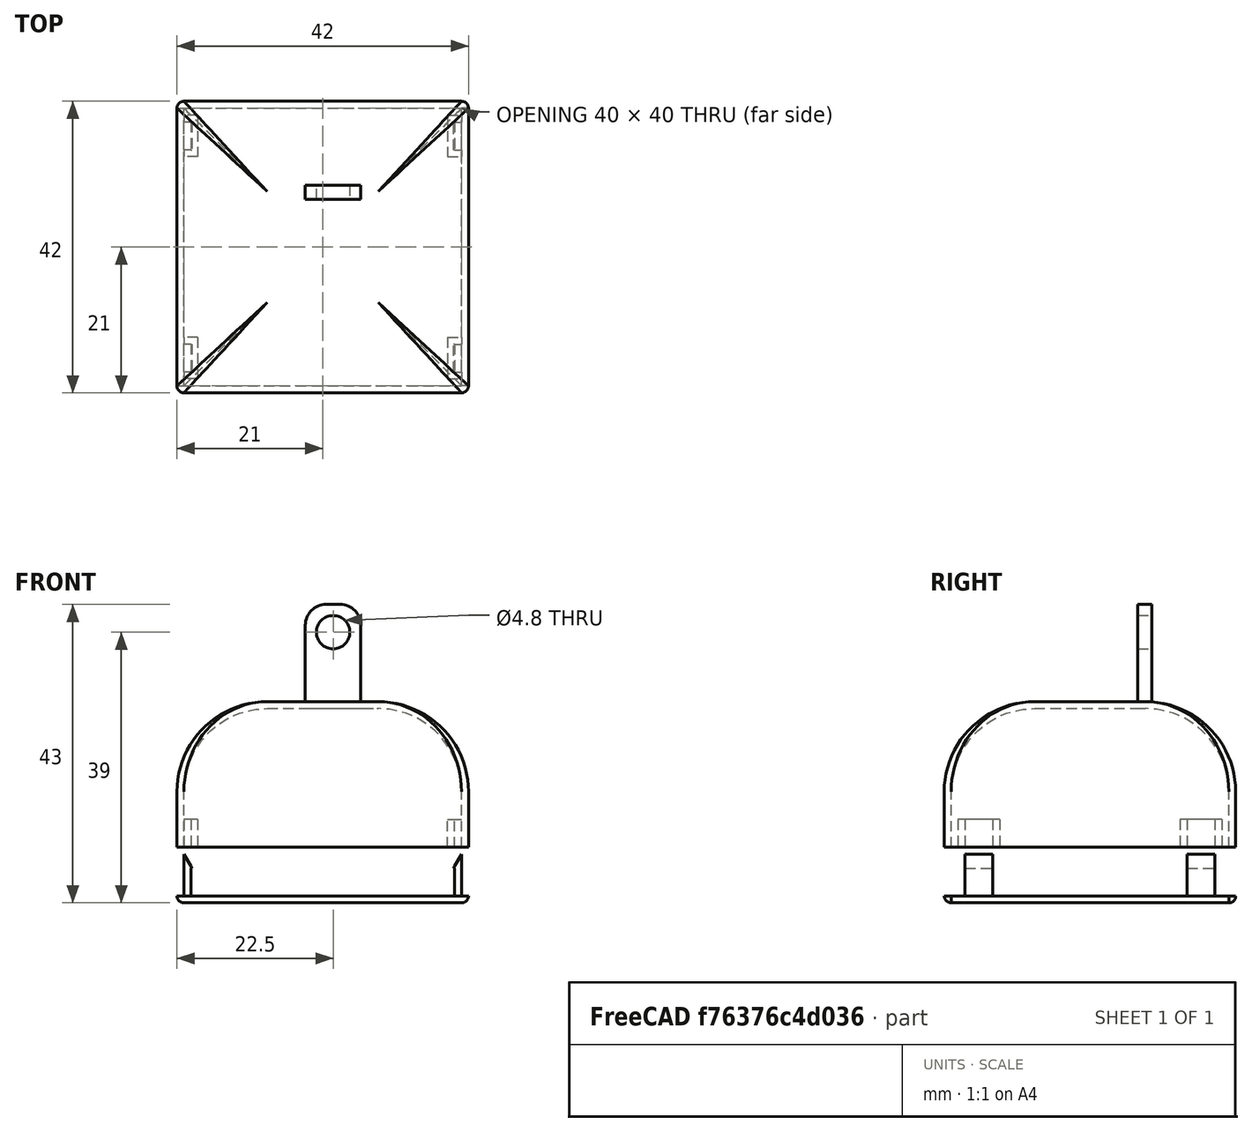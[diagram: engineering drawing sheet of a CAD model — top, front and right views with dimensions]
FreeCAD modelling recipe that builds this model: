
FCSTD DOCUMENT  (FreeCAD 0.21R33771 (Git))
Label: paw draft
License: All rights reserved
LicenseURL: https://en.wikipedia.org/wiki/All_rights_reserved
objects: Part::Box×24, Part::Cut×9, Part::MultiFuse×6, Part::Fillet×2, Part::Thickness×2, Part::Cylinder×1, Part::MultiCommon×1
note: 45 computed .brp shape members not serialized (recipe doc carries the construction recipe); baked Part::Feature solids carry a one-line shape summary decoded from their .brp

FEATURE [Part::Box] Box053  label="azeazeaze002"
  AttacherType = Attacher::AttachEngine3D
  Height = 15
  Length = 8
  Width = 2
FEATURE [Part::Box] Box055  label="Cube037"
  AttacherType = Attacher::AttachEngine3D
  Height = 1
  Length = 42
  Placement = pos=(-1,-1,-1) rot=(0,0,1;0rad)
  Width = 42
FEATURE [Part::Box] Box056  label="paw001"
  AttacherType = Attacher::AttachEngine3D
  Height = 20
  Length = 40
  Width = 40
FEATURE [Part::Box] Box057  label="Cube038"
  AttacherType = Attacher::AttachEngine3D
  Height = 6
  Length = 2
  Width = 4
FEATURE [Part::Box] Box058  label="Cube039"
  AttacherType = Attacher::AttachEngine3D
  Height = 4
  Length = 1
  Placement = pos=(1,0,1) rot=(0,0,1;0rad)
  Width = 4
FEATURE [Part::Box] Box059  label="Cube040"
  AttacherType = Attacher::AttachEngine3D
  Height = 6
  Length = 2
  Width = 4
FEATURE [Part::Box] Box060  label="Cube041"
  AttacherType = Attacher::AttachEngine3D
  Height = 4
  Length = 1
  Placement = pos=(1,0,1) rot=(0,0,1;0rad)
  Width = 4
FEATURE [Part::Box] Box061  label="Cube042"
  AttacherType = Attacher::AttachEngine3D
  Height = 6
  Length = 2
  Width = 4
FEATURE [Part::Box] Box062  label="Cube043"
  AttacherType = Attacher::AttachEngine3D
  Height = 4
  Length = 1
  Placement = pos=(1,0,1) rot=(0,0,1;0rad)
  Width = 4
FEATURE [Part::Box] Box063  label="Cube044"
  AttacherType = Attacher::AttachEngine3D
  Height = 6
  Length = 2
  Width = 4
FEATURE [Part::Box] Box064  label="Cube045"
  AttacherType = Attacher::AttachEngine3D
  Height = 4
  Length = 1
  Placement = pos=(1,0,1) rot=(0,0,1;0rad)
  Width = 4
FEATURE [Part::Box] Box065  label="paw002"
  AttacherType = Attacher::AttachEngine3D
  Height = 20
  Length = 40
  Width = 40
FEATURE [Part::Box] Box066  label="Cube046"
  AttacherType = Attacher::AttachEngine3D
  Height = 4
  Length = 2
  Placement = pos=(1,0,1) rot=(0,0,-1;0.523599rad)
  Width = 3
FEATURE [Part::Box] Box067  label="Cube047"
  AttacherType = Attacher::AttachEngine3D
  Height = 4
  Length = 1
  Placement = pos=(1,0,1) rot=(0,0,1;0rad)
  Width = 6
FEATURE [Part::Box] Box068  label="Cube048"
  AttacherType = Attacher::AttachEngine3D
  Height = 4
  Length = 1.2
  Placement = pos=(1,0,1) rot=(0,0,1;0rad)
  Width = 2
FEATURE [Part::Box] Box069  label="Cube049"
  AttacherType = Attacher::AttachEngine3D
  Height = 4
  Length = 2
  Placement = pos=(1,0,1) rot=(0,0,-1;0.523599rad)
  Width = 3
FEATURE [Part::Box] Box070  label="Cube050"
  AttacherType = Attacher::AttachEngine3D
  Height = 4
  Length = 1
  Placement = pos=(1,0,1) rot=(0,0,1;0rad)
  Width = 6
FEATURE [Part::Box] Box071  label="Cube051"
  AttacherType = Attacher::AttachEngine3D
  Height = 4
  Length = 1.2
  Placement = pos=(1,0,1) rot=(0,0,1;0rad)
  Width = 2
FEATURE [Part::Box] Box072  label="Cube052"
  AttacherType = Attacher::AttachEngine3D
  Height = 4
  Length = 2
  Placement = pos=(1,0,1) rot=(0,0,-1;0.523599rad)
  Width = 3
FEATURE [Part::Box] Box073  label="Cube053"
  AttacherType = Attacher::AttachEngine3D
  Height = 4
  Length = 1
  Placement = pos=(1,0,1) rot=(0,0,1;0rad)
  Width = 6
FEATURE [Part::Box] Box074  label="Cube054"
  AttacherType = Attacher::AttachEngine3D
  Height = 4
  Length = 1.2
  Placement = pos=(1,0,1) rot=(0,0,1;0rad)
  Width = 2
FEATURE [Part::Box] Box075  label="Cube055"
  AttacherType = Attacher::AttachEngine3D
  Height = 4
  Length = 2
  Placement = pos=(1,0,1) rot=(0,0,-1;0.523599rad)
  Width = 3
FEATURE [Part::Box] Box076  label="Cube056"
  AttacherType = Attacher::AttachEngine3D
  Height = 4
  Length = 1
  Placement = pos=(1,0,1) rot=(0,0,1;0rad)
  Width = 6
FEATURE [Part::Box] Box077  label="Cube057"
  AttacherType = Attacher::AttachEngine3D
  Height = 4
  Length = 1.2
  Placement = pos=(1,0,1) rot=(0,0,1;0rad)
  Width = 2
FEATURE [Part::Cut] Cut024
  Base = -> Box057
  Placement = pos=(38,7,1) rot=(1,0,0;1.5708rad)
  Tool = -> Box058
FEATURE [Part::Cut] Cut025
  Base = -> Box059
  Placement = pos=(38,39,1) rot=(1,0,0;1.5708rad)
  Tool = -> Box060
FEATURE [Part::Cut] Cut026
  Base = -> Box061
  Placement = pos=(2,7,5) rot=(0,0.707107,-0.707107;3.14159rad)
  Tool = -> Box062
FEATURE [Part::Cut] Cut027
  Base = -> Box063
  Placement = pos=(2,39,5) rot=(0,0.707107,-0.707107;3.14159rad)
  Tool = -> Box064
FEATURE [Part::Cylinder] Cylinder014  label="Cylindre014"
  Angle = 360
  AttacherType = Attacher::AttachEngine3D
  FirstAngle = 0
  Height = 10
  Placement = pos=(4,4,11) rot=(1,0,0;1.5708rad)
  Radius = 2.4
  SecondAngle = 0
FEATURE [Part::Cut] Cut022
  Base = -> Box053
  Placement = pos=(17.5,26.9,86) rot=(0,0,1;0rad)
  Tool = -> Cylinder014
FEATURE [Part::Fillet] Fillet005
  Base = -> Cut022
  Edges = 2 edges r=3: [Edge2,Edge10]
  Placement = pos=(0,0,-65) rot=(0,0,1;0rad)
FEATURE [Part::Fillet] Fillet007
  Base = -> Box056
  Edges = 4 edges r=12: [Edge2,Edge6,Edge10,Edge12]
  Placement = pos=(0,0,1) rot=(0,0,1;0rad)
FEATURE [Part::MultiFuse] Fusion022
  Shapes = -> [Box067,Box068]
FEATURE [Part::Cut] Cut028
  Base = -> Fusion022
  Placement = pos=(-1,1,0) rot=(-1,0,0;1.5708rad)
  Tool = -> Box066
FEATURE [Part::MultiFuse] Fusion023
  Shapes = -> [Box070,Box071]
FEATURE [Part::Cut] Cut029
  Base = -> Fusion023
  Placement = pos=(-1,33,7e-15) rot=(-1,0,0;1.5708rad)
  Tool = -> Box069
FEATURE [Part::MultiFuse] Fusion024
  Shapes = -> [Box073,Box074]
FEATURE [Part::Cut] Cut030
  Base = -> Fusion024
  Placement = pos=(41,7,1e-15) rot=(0,0.707107,-0.707107;3.14159rad)
  Tool = -> Box072
FEATURE [Part::MultiFuse] Fusion025
  Shapes = -> [Box076,Box077]
FEATURE [Part::Cut] Cut031
  Base = -> Fusion025
  Placement = pos=(41,39,8e-15) rot=(0,0.707107,-0.707107;3.14159rad)
  Tool = -> Box075
FEATURE [Part::Thickness] Thickness007
  Faces = -> Box065 [Face6]
  Intersection = false
  Join = 0
  Mode = 0
  SelfIntersection = false
  Value = 1
FEATURE [Part::MultiCommon] Common001
  Placement = pos=(0,0,-6) rot=(0,0,1;0rad)
  Shapes = -> [Box055,Thickness007]
FEATURE [Part::MultiFuse] Fusion026  label="Paw side"
  Shapes = -> [Common001,Cut028,Cut029,Cut030,Cut031]
FEATURE [Part::Thickness] Thickness008
  Faces = -> Fillet007 [Face4]
  Intersection = false
  Join = 0
  Mode = 0
  SelfIntersection = false
  Value = 1
FEATURE [Part::MultiFuse] Fusion021  label="Paw body"
  Shapes = -> [Fillet005,Thickness008,Cut027,Cut026,Cut025,Cut024]
